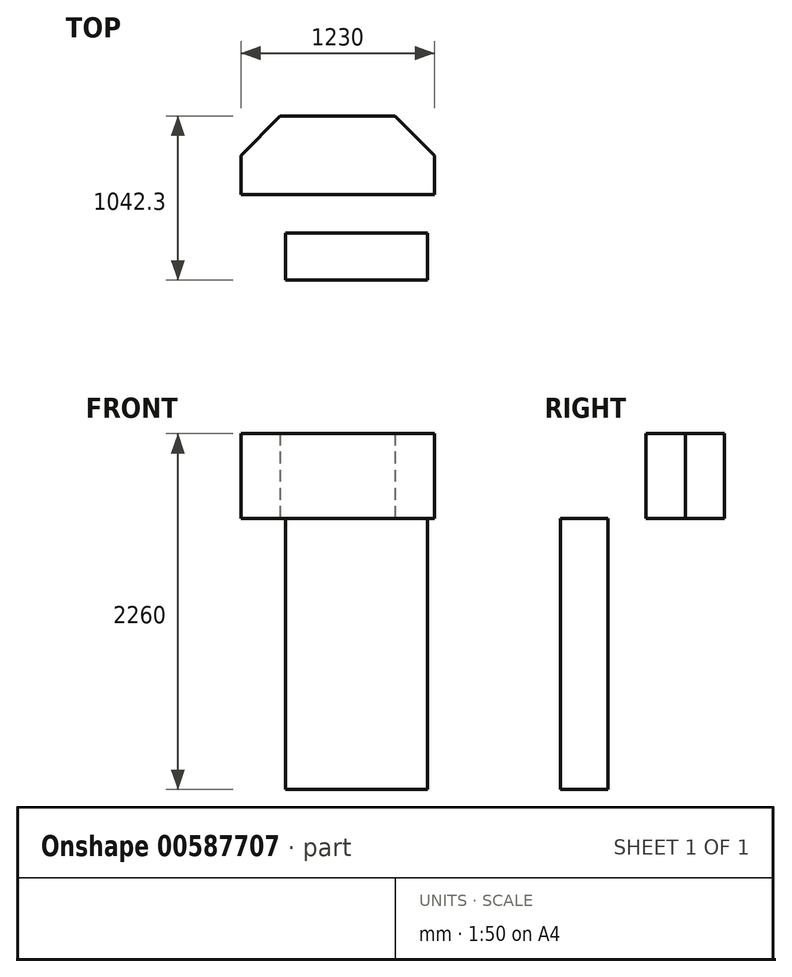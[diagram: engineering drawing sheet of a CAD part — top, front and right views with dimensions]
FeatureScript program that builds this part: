
annotation { "Feature Type Name" : "Feature", "Feature Type Description" : "" }
export const myFeature = defineFeature(function(context is Context, id is Id, definition is map)
    precondition{}
    {
        {
            var Q0;
            Q0=qCreatedBy(makeId("Top.planeOp"),FACE);
            var sketch = newSketch(context, id + "F0", { "sketchPlane" : qUnion([Q0])});
            skLineSegment(sketch, "E0", {"start": v(-250, -154.24) * mm, "end": v(980, -154.24) * mm});
            skLineSegment(sketch, "E1", {"start": v(980, -154.24) * mm, "end": v(980, 95.76) * mm});
            skLineSegment(sketch, "E2", {"start": v(730, 345.76) * mm, "end": v(0, 345.76) * mm});
            skLineSegment(sketch, "E3", {"start": v(-250, 95.76) * mm, "end": v(-250, -154.24) * mm});
            skLineSegment(sketch, "E4", {"start": v(-250, 95.76) * mm, "end": v(0, 345.76) * mm});
            skLineSegment(sketch, "E5", {"start": v(730, 345.76) * mm, "end": v(980, 95.76) * mm});
            skSolve(sketch);
        }
        {
            var Q0;
            Q0=makeQuery(id+"F0.imprint","IMPRINT",FACE,{"disambiguationData":[TD([[makeQuery(id+"F0.imprint","IMPRINT",EDGE,{"derivedFrom":sQuery(id+"F0.wireOp",EDGE,"E0")}),1.0]])]});
            extrude(context, id + "F1", {"entities" : qUnion([Q0]), "depth" : 540 * mm, "offsetDistance" : 25 * mm});
        }
        {
            var Q0;
            Q0=makeQuery(id+"F1.opExtrude","CAP_FACE",FACE,{"disambiguationData":[OSD([sQuery(id+"F0.wireOp",EDGE,"E0"),sQuery(id+"F0.wireOp",EDGE,"E1"),sQuery(id+"F0.wireOp",EDGE,"E2"),sQuery(id+"F0.wireOp",EDGE,"E3"),sQuery(id+"F0.wireOp",EDGE,"E4"),sQuery(id+"F0.wireOp",EDGE,"E5")])],"isStart":true});
            var sketch = newSketch(context, id + "F2", { "sketchPlane" : qUnion([Q0])});
            skLineSegment(sketch, "E6.bottom", {"start": v(34.18, 396.54) * mm, "end": v(934.18, 396.54) * mm});
            skLineSegment(sketch, "E6.top", {"start": v(34.18, 696.54) * mm, "end": v(934.18, 696.54) * mm});
            skLineSegment(sketch, "E6.left", {"start": v(34.18, 396.54) * mm, "end": v(34.18, 696.54) * mm});
            skLineSegment(sketch, "E6.right", {"start": v(934.18, 396.54) * mm, "end": v(934.18, 696.54) * mm});
            skSolve(sketch);
        }
        {
            var Q0;
            Q0=makeQuery(id+"F2.imprint","IMPRINT",FACE,{"disambiguationData":[TD([[makeQuery(id+"F2.imprint","IMPRINT",EDGE,{"derivedFrom":sQuery(id+"F2.wireOp",EDGE,"E6.bottom")}),1.0]])]});
            extrude(context, id + "F3", {"entities" : qUnion([Q0]), "depth" : 1720 * mm, "offsetDistance" : 25 * mm});
        }
    });
